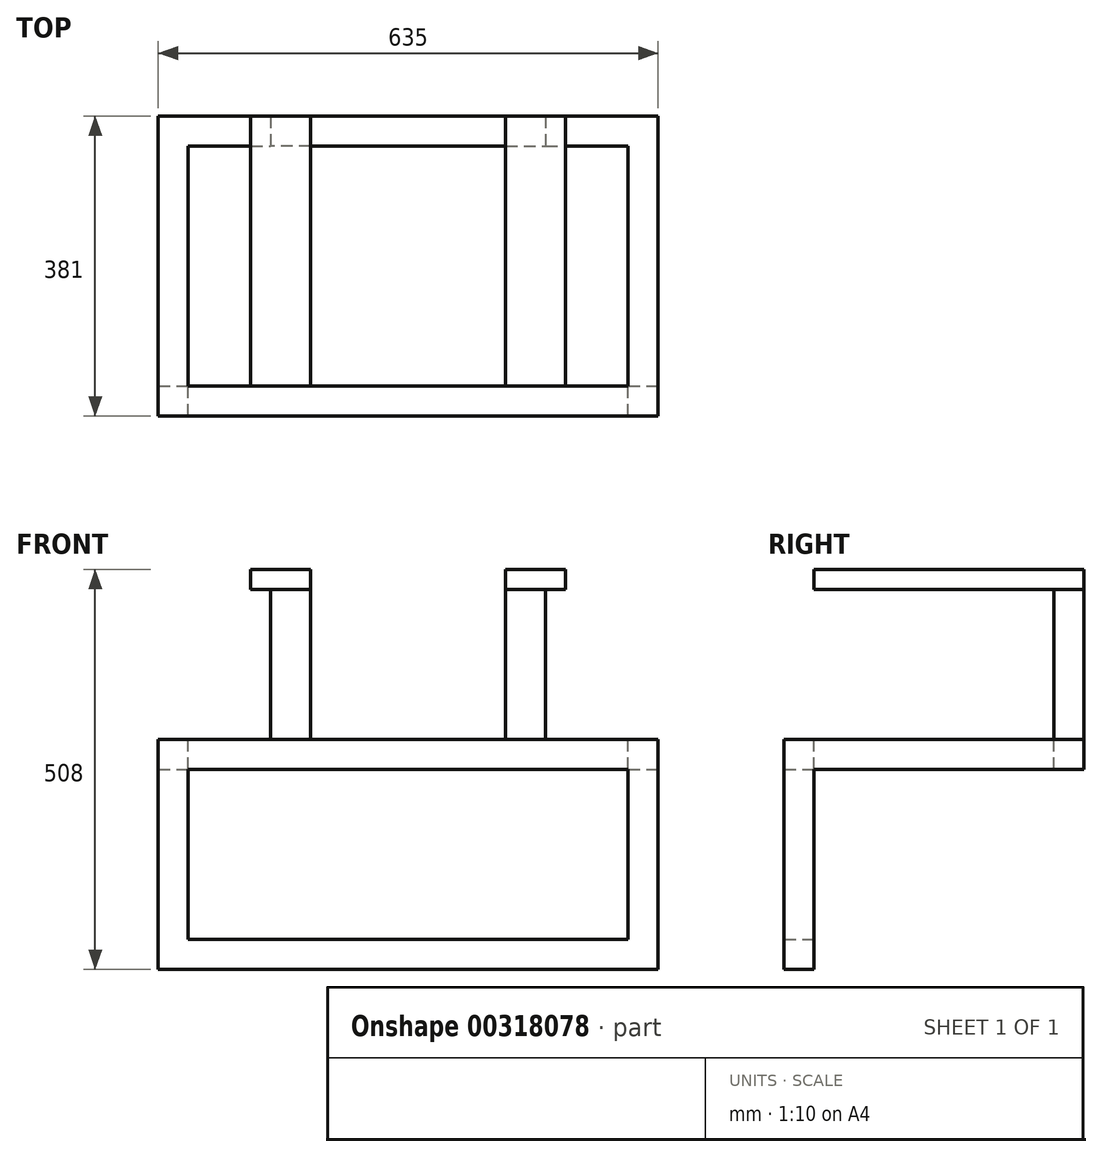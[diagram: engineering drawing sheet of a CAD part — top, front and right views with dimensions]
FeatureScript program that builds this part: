
annotation { "Feature Type Name" : "Feature", "Feature Type Description" : "" }
export const myFeature = defineFeature(function(context is Context, id is Id, definition is map)
    precondition{}
    {
        {
            var Q0;
            Q0=qCreatedBy(makeId("Front.planeOp"),FACE);
            var sketch = newSketch(context, id + "F0", { "sketchPlane" : qUnion([Q0])});
            skLineSegment(sketch, "E0.0", {"start": v(38.1, 38.1) * mm, "end": v(596.9, 38.1) * mm});
            skLineSegment(sketch, "E0.2", {"start": v(0, 254) * mm, "end": v(635, 254) * mm});
            skLineSegment(sketch, "E1.0.1.4", {"start": v(0, 292.1) * mm, "end": v(635, 292.1) * mm});
            skLineSegment(sketch, "E1.0.1.5", {"start": v(38.1, 38.1) * mm, "end": v(38.1, 971.55) * mm});
            skLineSegment(sketch, "E1.0.1.7", {"start": v(596.9, 38.1) * mm, "end": v(596.9, 971.55) * mm});
            skLineSegment(sketch, "E2.top", {"start": v(0, 0) * mm, "end": v(635, 0) * mm});
            skLineSegment(sketch, "E2.left", {"start": v(0, 971.55) * mm, "end": v(0, 0) * mm});
            skLineSegment(sketch, "E2.right", {"start": v(635, 971.55) * mm, "end": v(635, 0) * mm});
            skLineSegment(sketch, "E3", {"start": v(0, 971.55) * mm, "end": v(38.1, 971.55) * mm});
            skLineSegment(sketch, "E4", {"start": v(596.9, 971.55) * mm, "end": v(635, 971.55) * mm});
            skLineSegment(sketch, "E5", {"start": v(142.88, 292.1) * mm, "end": v(142.88, 482.6) * mm});
            skLineSegment(sketch, "E6", {"start": v(193.68, 482.6) * mm, "end": v(117.48, 482.6) * mm});
            skLineSegment(sketch, "E7", {"start": v(117.48, 482.6) * mm, "end": v(117.48, 508) * mm});
            skLineSegment(sketch, "E8", {"start": v(117.48, 508) * mm, "end": v(193.68, 508) * mm});
            skLineSegment(sketch, "E9", {"start": v(193.68, 508) * mm, "end": v(193.68, 292.1) * mm});
            skLineSegment(sketch, "E10", {"start": v(317.5, 0) * mm, "end": v(317.5, 971.55) * mm, "construction": true});
            skLineSegment(sketch, "E11.MirrorCS", {"start": v(517.53, 482.6) * mm, "end": v(517.53, 508) * mm});
            skLineSegment(sketch, "E12.MirrorCS", {"start": v(441.33, 482.6) * mm, "end": v(517.53, 482.6) * mm});
            skLineSegment(sketch, "E13.MirrorCS", {"start": v(441.33, 508) * mm, "end": v(441.33, 292.1) * mm});
            skLineSegment(sketch, "E14.MirrorCS", {"start": v(492.13, 292.1) * mm, "end": v(492.13, 482.6) * mm});
            skLineSegment(sketch, "E15.MirrorCS", {"start": v(517.53, 508) * mm, "end": v(441.33, 508) * mm});
            skSolve(sketch);
        }
        {
            var Q0;
            Q0=makeQuery(id+"F0.imprint","IMPRINT",FACE,{"disambiguationData":[TD([[makeQuery(id+"F0.imprint","IMPRINT",EDGE,{"derivedFrom":sQuery(id+"F0.wireOp",EDGE,"E0.0")}),-1.0]])]});
            var Q1;
            {var subQ0=sQuery(id+"F0.wireOp",EDGE,"E2.left");var subQ1=sQuery(id+"F0.wireOp",EDGE,"E0.2");var subQ2=makeQuery(id+"F0.imprint","INTERSECT",VERTEX,{"derivedFrom":[subQ1,subQ0]});Q1=makeQuery(id+"F0.imprint","IMPRINT",FACE,{"disambiguationData":[TD([[makeQuery(id+"F0.imprint","IMPRINT",EDGE,{"disambiguationData":[TD([[subQ2,-1.0]])],"derivedFrom":subQ1}),1.0]])]});}
            var Q2;
            {var subQ0=sQuery(id+"F0.wireOp",EDGE,"E1.0.1.5");var subQ1=sQuery(id+"F0.wireOp",EDGE,"E0.2");var subQ2=makeQuery(id+"F0.imprint","INTERSECT",VERTEX,{"derivedFrom":[subQ1,subQ0]});Q2=makeQuery(id+"F0.imprint","IMPRINT",FACE,{"disambiguationData":[TD([[makeQuery(id+"F0.imprint","IMPRINT",EDGE,{"disambiguationData":[TD([[subQ2,-1.0]])],"derivedFrom":subQ1}),1.0]])]});}
            var Q3;
            {var subQ0=sQuery(id+"F0.wireOp",EDGE,"E2.right");var subQ1=sQuery(id+"F0.wireOp",EDGE,"E0.2");var subQ2=makeQuery(id+"F0.imprint","INTERSECT",VERTEX,{"derivedFrom":[subQ1,subQ0]});Q3=makeQuery(id+"F0.imprint","IMPRINT",FACE,{"disambiguationData":[TD([[makeQuery(id+"F0.imprint","IMPRINT",EDGE,{"disambiguationData":[TD([[subQ2,1.0]])],"derivedFrom":subQ1}),1.0]])]});}
            extrude(context, id + "F1", {"entities" : qUnion([Q0, Q1, Q2, Q3]), "depth" : 38.1 * mm, "offsetDistance" : 25.4 * mm});
        }
        {
            var Q0;
            {var subQ0=sQuery(id+"F0.wireOp",EDGE,"E2.left");var subQ1=sQuery(id+"F0.wireOp",EDGE,"E0.2");var subQ2=makeQuery(id+"F0.imprint","INTERSECT",VERTEX,{"derivedFrom":[subQ1,subQ0]});Q0=makeQuery(id+"F0.imprint","IMPRINT",FACE,{"disambiguationData":[TD([[makeQuery(id+"F0.imprint","IMPRINT",EDGE,{"disambiguationData":[TD([[subQ2,-1.0]])],"derivedFrom":subQ1}),1.0]])]});}
            var Q1;
            {var subQ0=sQuery(id+"F0.wireOp",EDGE,"E2.right");var subQ1=sQuery(id+"F0.wireOp",EDGE,"E0.2");var subQ2=makeQuery(id+"F0.imprint","INTERSECT",VERTEX,{"derivedFrom":[subQ1,subQ0]});Q1=makeQuery(id+"F0.imprint","IMPRINT",FACE,{"disambiguationData":[TD([[makeQuery(id+"F0.imprint","IMPRINT",EDGE,{"disambiguationData":[TD([[subQ2,1.0]])],"derivedFrom":subQ1}),1.0]])]});}
            extrude(context, id + "F2", {"entities" : qUnion([Q0, Q1]), "operationType" : NewBodyOperationType.ADD, "oppositeDirection" : true, "depth" : 304.8 * mm, "offsetDistance" : 25.4 * mm});
        }
        {
            var Q0;
            {var subQ0=sQuery(id+"F0.wireOp",EDGE,"E1.0.1.5");var subQ1=sQuery(id+"F0.wireOp",EDGE,"E0.2");var subQ2=makeQuery(id+"F0.imprint","INTERSECT",VERTEX,{"derivedFrom":[subQ1,subQ0]});Q0=makeQuery(id+"F0.imprint","IMPRINT",FACE,{"disambiguationData":[TD([[makeQuery(id+"F0.imprint","IMPRINT",EDGE,{"disambiguationData":[TD([[subQ2,-1.0]])],"derivedFrom":subQ1}),1.0]])]});}
            var Q1;
            {var subQ0=sQuery(id+"F0.wireOp",EDGE,"E2.left");var subQ1=sQuery(id+"F0.wireOp",EDGE,"E0.2");var subQ2=makeQuery(id+"F0.imprint","INTERSECT",VERTEX,{"derivedFrom":[subQ1,subQ0]});Q1=makeQuery(id+"F0.imprint","IMPRINT",FACE,{"disambiguationData":[TD([[makeQuery(id+"F0.imprint","IMPRINT",EDGE,{"disambiguationData":[TD([[subQ2,-1.0]])],"derivedFrom":subQ1}),1.0]])]});}
            var Q2;
            {var subQ0=sQuery(id+"F0.wireOp",EDGE,"E2.right");var subQ1=sQuery(id+"F0.wireOp",EDGE,"E0.2");var subQ2=makeQuery(id+"F0.imprint","INTERSECT",VERTEX,{"derivedFrom":[subQ1,subQ0]});Q2=makeQuery(id+"F0.imprint","IMPRINT",FACE,{"disambiguationData":[TD([[makeQuery(id+"F0.imprint","IMPRINT",EDGE,{"disambiguationData":[TD([[subQ2,1.0]])],"derivedFrom":subQ1}),1.0]])]});}
            extrude(context, id + "F3", {"entities" : qUnion([Q0, Q1, Q2]), "operationType" : NewBodyOperationType.ADD, "oppositeDirection" : true, "depth" : 342.9 * mm, "offsetDistance" : 25.4 * mm, "hasSecondDirection" : true, "secondDirectionOppositeDirection" : true, "secondDirectionDepth" : 304.8 * mm});
        }
        {
            var Q0;
            {var subQ0=sQuery(id+"F0.wireOp",EDGE,"E5");Q0=makeQuery(id+"F0.imprint","IMPRINT",FACE,{"disambiguationData":[TD([[makeQuery(id+"F0.imprint","IMPRINT",EDGE,{"derivedFrom":subQ0}),-1.0]])]});}
            var Q1;
            {var subQ3=sQuery(id+"F0.wireOp",EDGE,"E14.MirrorCS");Q1=makeQuery(id+"F0.imprint","IMPRINT",FACE,{"disambiguationData":[TD([[makeQuery(id+"F0.imprint","IMPRINT",EDGE,{"derivedFrom":subQ3}),1.0]])]});}
            extrude(context, id + "F4", {"entities" : qUnion([Q0, Q1]), "operationType" : NewBodyOperationType.ADD, "oppositeDirection" : true, "depth" : 342.9 * mm, "offsetDistance" : 25.4 * mm, "hasSecondDirection" : true, "secondDirectionOppositeDirection" : true, "secondDirectionDepth" : 304.8 * mm});
        }
        {
            var Q0;
            {var subQ1=sQuery(id+"F0.wireOp",EDGE,"E7");Q0=makeQuery(id+"F0.imprint","IMPRINT",FACE,{"disambiguationData":[TD([[makeQuery(id+"F0.imprint","IMPRINT",EDGE,{"derivedFrom":subQ1}),-1.0]])]});}
            var Q1;
            {var subQ4=sQuery(id+"F0.wireOp",EDGE,"E11.MirrorCS");Q1=makeQuery(id+"F0.imprint","IMPRINT",FACE,{"disambiguationData":[TD([[makeQuery(id+"F0.imprint","IMPRINT",EDGE,{"derivedFrom":subQ4}),1.0]])]});}
            extrude(context, id + "F5", {"entities" : qUnion([Q0, Q1]), "operationType" : NewBodyOperationType.ADD, "oppositeDirection" : true, "depth" : 342.9 * mm, "offsetDistance" : 25.4 * mm});
        }
    });
